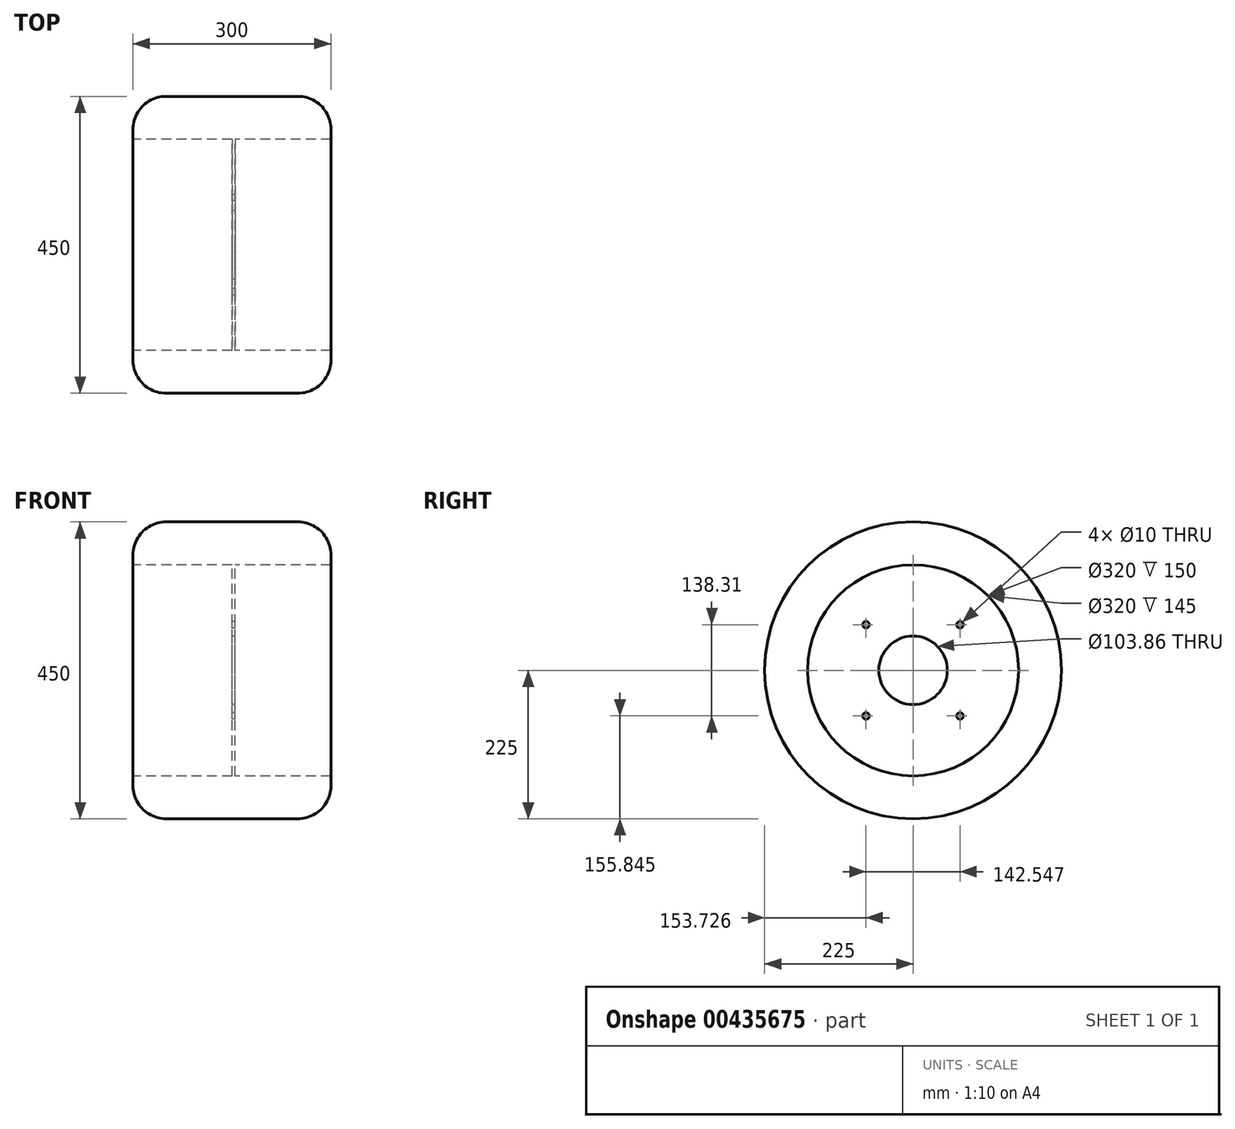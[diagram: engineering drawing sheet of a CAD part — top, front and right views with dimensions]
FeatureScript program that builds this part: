
annotation { "Feature Type Name" : "Feature", "Feature Type Description" : "" }
export const myFeature = defineFeature(function(context is Context, id is Id, definition is map)
    precondition{}
    {
        {
            var Q0;
            Q0=qCreatedBy(makeId("Right.planeOp"),FACE);
            var sketch = newSketch(context, id + "F0", { "sketchPlane" : qUnion([Q0])});
            skCircle(sketch, "E0", {"center": v(0, 0) * mm, "radius": 225 * mm});
            skCircle(sketch, "E1", {"center": v(0, 0) * mm, "radius": 160 * mm});
            skCircle(sketch, "E2", {"center": v(0, 0) * mm, "radius": 99.3 * mm});
            skCircle(sketch, "E3", {"center": v(0, 0) * mm, "radius": 51.93 * mm});
            skLineSegment(sketch, "E4.bottom", {"start": v(-71.27, 69.16) * mm, "end": v(71.27, 69.16) * mm});
            skLineSegment(sketch, "E4.top", {"start": v(-71.27, -69.16) * mm, "end": v(71.27, -69.16) * mm});
            skLineSegment(sketch, "E4.left", {"start": v(-71.27, 69.16) * mm, "end": v(-71.27, -69.16) * mm});
            skLineSegment(sketch, "E4.right", {"start": v(71.27, 69.16) * mm, "end": v(71.27, -69.16) * mm});
            skCircle(sketch, "E5", {"center": v(-71.27, 69.16) * mm, "radius": 5 * mm});
            skCircle(sketch, "E6", {"center": v(71.27, 69.16) * mm, "radius": 5 * mm});
            skCircle(sketch, "E7", {"center": v(71.27, -69.16) * mm, "radius": 5 * mm});
            skCircle(sketch, "E8", {"center": v(-71.27, -69.16) * mm, "radius": 5 * mm});
            skSolve(sketch);
        }
        {
            var Q0;
            Q0 = qSketchRegion(id + "F0", true);
            extrude(context, id + "F1", {"entities" : qUnion([Q0]), "endBound" : BoundingType.SYMMETRIC, "depth" : 300 * mm});
        }
        {
            var Q0;
            Q0=makeQuery(id+"F1.opExtrude","CAP_EDGE",EDGE,{"disambiguationData":[OSD([sQuery(id+"F0.wireOp",EDGE,"E0")])],"isStart":false});
            var Q1;
            Q1=makeQuery(id+"F1.opExtrude","SWEPT_FACE",FACE,{"disambiguationData":[OSD([sQuery(id+"F0.wireOp",EDGE,"E0")])]});
            fillet(context, id + "F2", {"entities" : qUnion([Q0, Q1]), "radius" : 50 * mm, "tangentPropagation" : true, "allowEdgeOverflow" : false});
        }
        {
            var Q0;
            Q0=makeQuery(id+"F0.imprint","IMPRINT",FACE,{"disambiguationData":[TD([[makeQuery(id+"F0.imprint","IMPRINT",EDGE,{"derivedFrom":sQuery(id+"F0.wireOp",EDGE,"E1")}),1.0]])]});
            var Q1;
            {var subQ0=sQuery(id+"F0.wireOp",EDGE,"E5");var subQ1=sQuery(id+"F0.wireOp",EDGE,"E2");var subQ2=makeQuery(id+"F0.imprint","INTERSECT",VERTEX,{"disambiguationData":[OD(1.0)],"derivedFrom":[subQ1,subQ0]});Q1=makeQuery(id+"F0.imprint","IMPRINT",FACE,{"disambiguationData":[TD([[makeQuery(id+"F0.imprint","IMPRINT",EDGE,{"disambiguationData":[TD([[subQ2,-1.0]])],"derivedFrom":subQ1}),1.0]])]});}
            var Q2;
            {var subQ0=sQuery(id+"F0.wireOp",EDGE,"E6");var subQ1=sQuery(id+"F0.wireOp",EDGE,"E2");var subQ2=makeQuery(id+"F0.imprint","INTERSECT",VERTEX,{"disambiguationData":[OD(1.0)],"derivedFrom":[subQ1,subQ0]});Q2=makeQuery(id+"F0.imprint","IMPRINT",FACE,{"disambiguationData":[TD([[makeQuery(id+"F0.imprint","IMPRINT",EDGE,{"disambiguationData":[TD([[subQ2,-1.0]])],"derivedFrom":subQ1}),1.0]])]});}
            var Q3;
            {var subQ0=sQuery(id+"F0.wireOp",EDGE,"E8");var subQ1=sQuery(id+"F0.wireOp",EDGE,"E2");var subQ2=makeQuery(id+"F0.imprint","INTERSECT",VERTEX,{"disambiguationData":[OD(1.0)],"derivedFrom":[subQ1,subQ0]});Q3=makeQuery(id+"F0.imprint","IMPRINT",FACE,{"disambiguationData":[TD([[makeQuery(id+"F0.imprint","IMPRINT",EDGE,{"disambiguationData":[TD([[subQ2,-1.0]])],"derivedFrom":subQ1}),1.0]])]});}
            var Q4;
            Q4=makeQuery(id+"F0.imprint","IMPRINT",FACE,{"disambiguationData":[TD([[makeQuery(id+"F0.imprint","IMPRINT",EDGE,{"derivedFrom":sQuery(id+"F0.wireOp",EDGE,"E3")}),-1.0]])]});
            var Q5;
            {var subQ0=sQuery(id+"F0.wireOp",EDGE,"E6");var subQ1=sQuery(id+"F0.wireOp",EDGE,"E2");var subQ2=makeQuery(id+"F0.imprint","INTERSECT",VERTEX,{"disambiguationData":[OD(0.0)],"derivedFrom":[subQ1,subQ0]});Q5=makeQuery(id+"F0.imprint","IMPRINT",FACE,{"disambiguationData":[TD([[makeQuery(id+"F0.imprint","IMPRINT",EDGE,{"disambiguationData":[TD([[subQ2,1.0]])],"derivedFrom":subQ1}),1.0]])]});}
            extrude(context, id + "F3", {"entities" : qUnion([Q0, Q1, Q2, Q3, Q4, Q5]), "operationType" : NewBodyOperationType.ADD, "depth" : 5 * mm});
        }
    });
